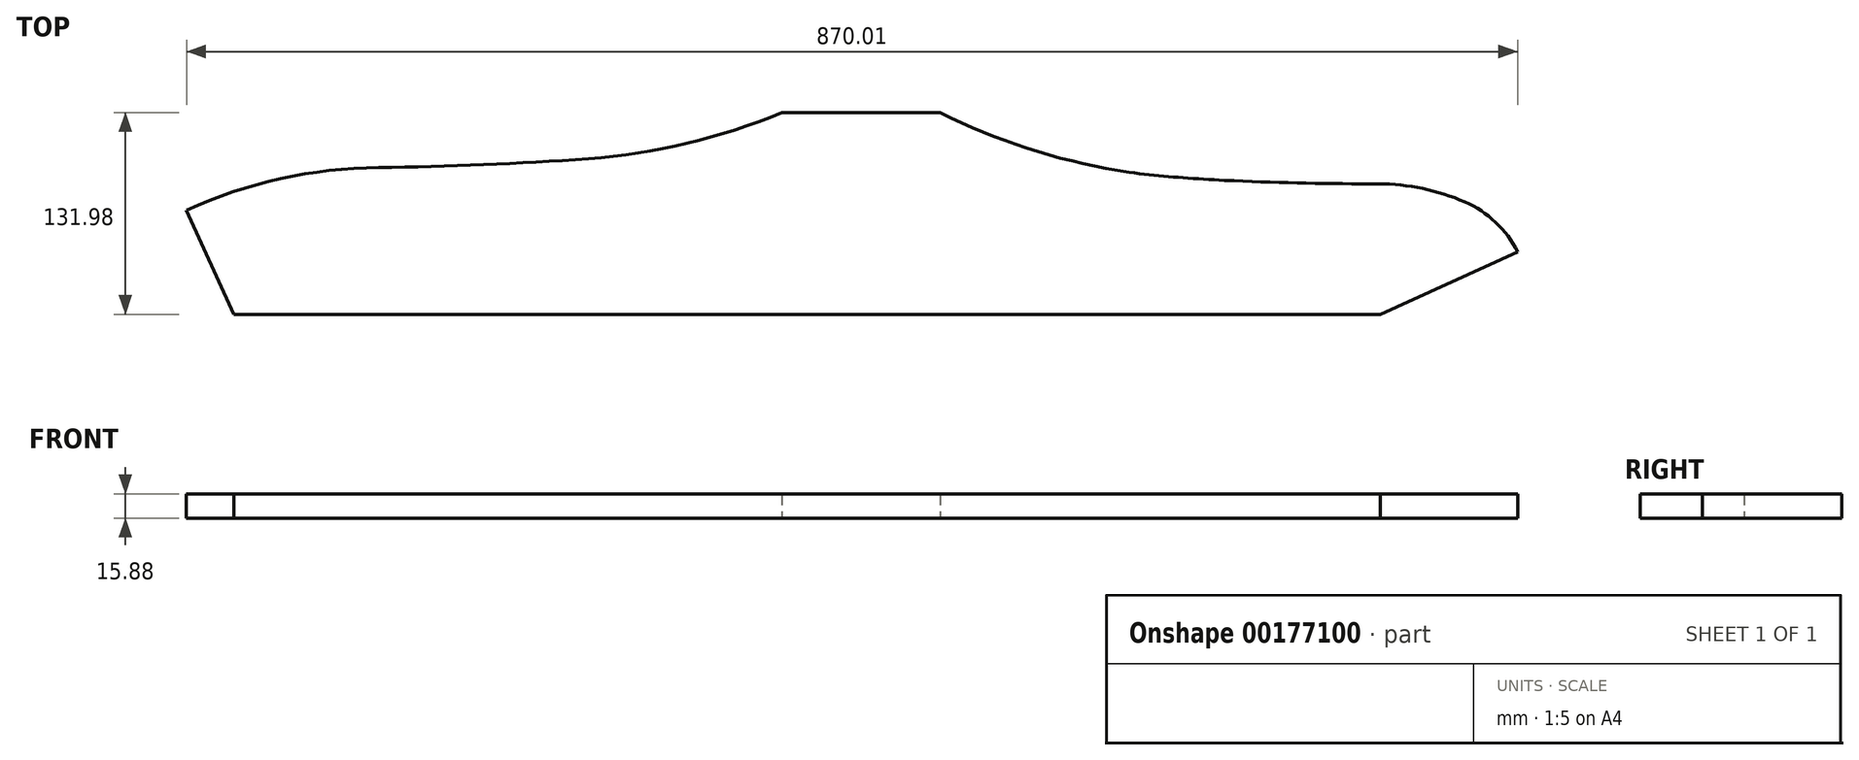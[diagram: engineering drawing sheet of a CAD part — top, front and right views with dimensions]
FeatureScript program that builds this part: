
annotation { "Feature Type Name" : "Feature", "Feature Type Description" : "" }
export const myFeature = defineFeature(function(context is Context, id is Id, definition is map)
    precondition{}
    {
        {
            var Q0;
            Q0=qCreatedBy(makeId("Top.planeOp"),FACE);
            var sketch = newSketch(context, id + "F0", { "sketchPlane" : qUnion([Q0])});
            skLineSegment(sketch, "E0", {"start": v(-374.65, 0) * mm, "end": v(374.65, 0) * mm});
            skLineSegment(sketch, "E1", {"start": v(0, 0) * mm, "end": v(0, 133.35) * mm, "construction": true});
            skLineSegment(sketch, "E2", {"start": v(-405.72, 68.18) * mm, "end": v(-374.65, 0) * mm});
            skLineSegment(sketch, "E3", {"start": v(-374.65, 0) * mm, "end": v(-374.65, 68.18) * mm, "construction": true});
            skArc(sketch, "E4", {"start": v(-280, 96.13) * mm, "mid": v(-344.33, 88.73) * mm, "end": v(-405.72, 68.18) * mm});
            skArc(sketch, "E5", {"start": v(-280, 96.13) * mm, "mid": v(-211.43, 97.92) * mm, "end": v(-142.94, 101.89) * mm});
            skArc(sketch, "E6", {"start": v(-142.94, 101.89) * mm, "mid": v(-78.64, 111.87) * mm, "end": v(-16.76, 131.98) * mm});
            skLineSegment(sketch, "E7", {"start": v(-16.76, 131.98) * mm, "end": v(86.99, 131.98) * mm});
            skArc(sketch, "E8", {"start": v(86.99, 131.98) * mm, "mid": v(143.44, 108.76) * mm, "end": v(202.73, 94.26) * mm});
            skArc(sketch, "E9", {"start": v(278.8, 87.4) * mm, "mid": v(326.09, 85.9) * mm, "end": v(373.4, 85.35) * mm});
            skFitSpline(sketch, "E10", {"points": [v(202.73, 94.26) * mm, v(229.16, 90.8) * mm, v(253.45, 88.82) * mm, v(278.8, 87.4) * mm], "startDerivative": vector(92.51, -15.73) * mm, "endDerivative": vector(69.54, -2.92) * mm});
            skArc(sketch, "E11", {"start": v(429.76, 73.56) * mm, "mid": v(402.19, 82.35) * mm, "end": v(373.4, 85.35) * mm});
            skArc(sketch, "E12", {"start": v(464.29, 40.85) * mm, "mid": v(449.9, 60.23) * mm, "end": v(429.76, 73.56) * mm});
            skLineSegment(sketch, "E13", {"start": v(374.65, 0) * mm, "end": v(464.29, 40.85) * mm});
            skLineSegment(sketch, "E14", {"start": v(374.65, 0) * mm, "end": v(374.65, 56.73) * mm, "construction": true});
            skSolve(sketch);
        }
        {
            var Q0;
            Q0 = qSketchRegion(id + "F0", true);
            extrude(context, id + "F1", {"entities" : qUnion([Q0]), "depth" : 15.88 * mm});
        }
    });
